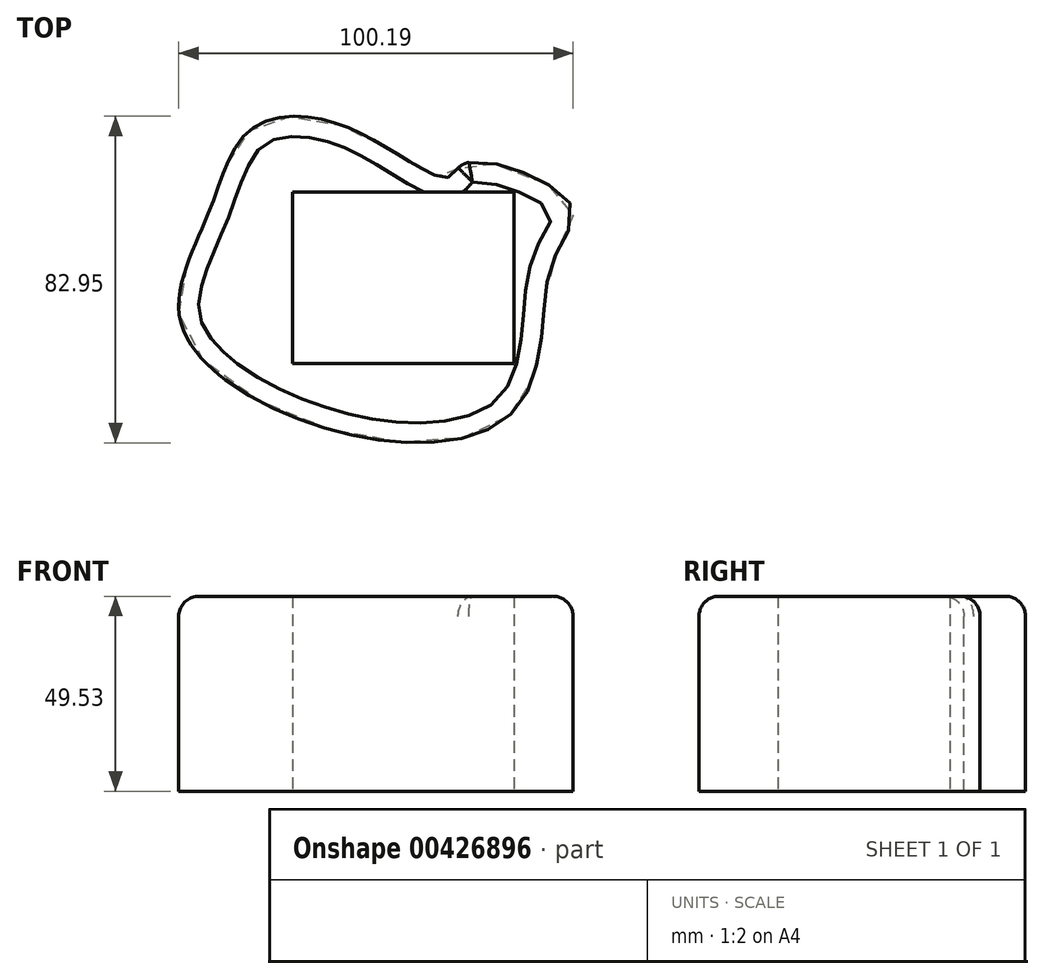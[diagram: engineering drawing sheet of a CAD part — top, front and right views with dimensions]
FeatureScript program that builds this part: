
annotation { "Feature Type Name" : "Feature", "Feature Type Description" : "" }
export const myFeature = defineFeature(function(context is Context, id is Id, definition is map)
    precondition{}
    {
        {
            var Q0;
            Q0=qCreatedBy(makeId("Top.planeOp"),FACE);
            var sketch = newSketch(context, id + "F0", { "sketchPlane" : qUnion([Q0])});
            skLineSegment(sketch, "E0.bottom", {"start": v(-30.95, 24.33) * mm, "end": v(25.3, 24.33) * mm});
            skLineSegment(sketch, "E0.top", {"start": v(-30.95, -19.27) * mm, "end": v(25.3, -19.27) * mm});
            skLineSegment(sketch, "E0.left", {"start": v(-30.95, 24.33) * mm, "end": v(-30.95, -19.27) * mm});
            skLineSegment(sketch, "E0.right", {"start": v(25.3, 24.33) * mm, "end": v(25.3, -19.27) * mm});
            skFitSpline(sketch, "E1", {"points": [v(-52.37, 18.88) * mm, v(-41.47, 40.3) * mm, v(-16.35, 40.5) * mm, v(8.37, 28.03) * mm, v(13.24, 31.73) * mm, v(39.52, 21.41) * mm, v(35.62, 7.98) * mm, v(32.12, -13.43) * mm, v(23.17, -33.29) * mm, v(-17.13, -37.18) * mm, v(-58.99, -10.12) * mm, v(-52.37, 18.88) * mm]});
            skSolve(sketch);
        }
        {
            var Q0;
            Q0=makeQuery(id+"F0.imprint","IMPRINT",FACE,{"disambiguationData":[TD([[makeQuery(id+"F0.imprint","IMPRINT",EDGE,{"derivedFrom":sQuery(id+"F0.wireOp",EDGE,"E0.bottom")}),1.0]])]});
            extrude(context, id + "F1", {"entities" : qUnion([Q0]), "depth" : 49.53 * mm});
        }
        {
            var Q0;
            Q0=makeQuery(id+"F1.opExtrude","CAP_EDGE",EDGE,{"disambiguationData":[OSD([sQuery(id+"F0.wireOp",EDGE,"E1")])],"isStart":false});
            fillet(context, id + "F2", {"entities" : qUnion([Q0]), "radius" : 5.08 * mm, "tangentPropagation" : true, "allowEdgeOverflow" : false});
        }
    });
